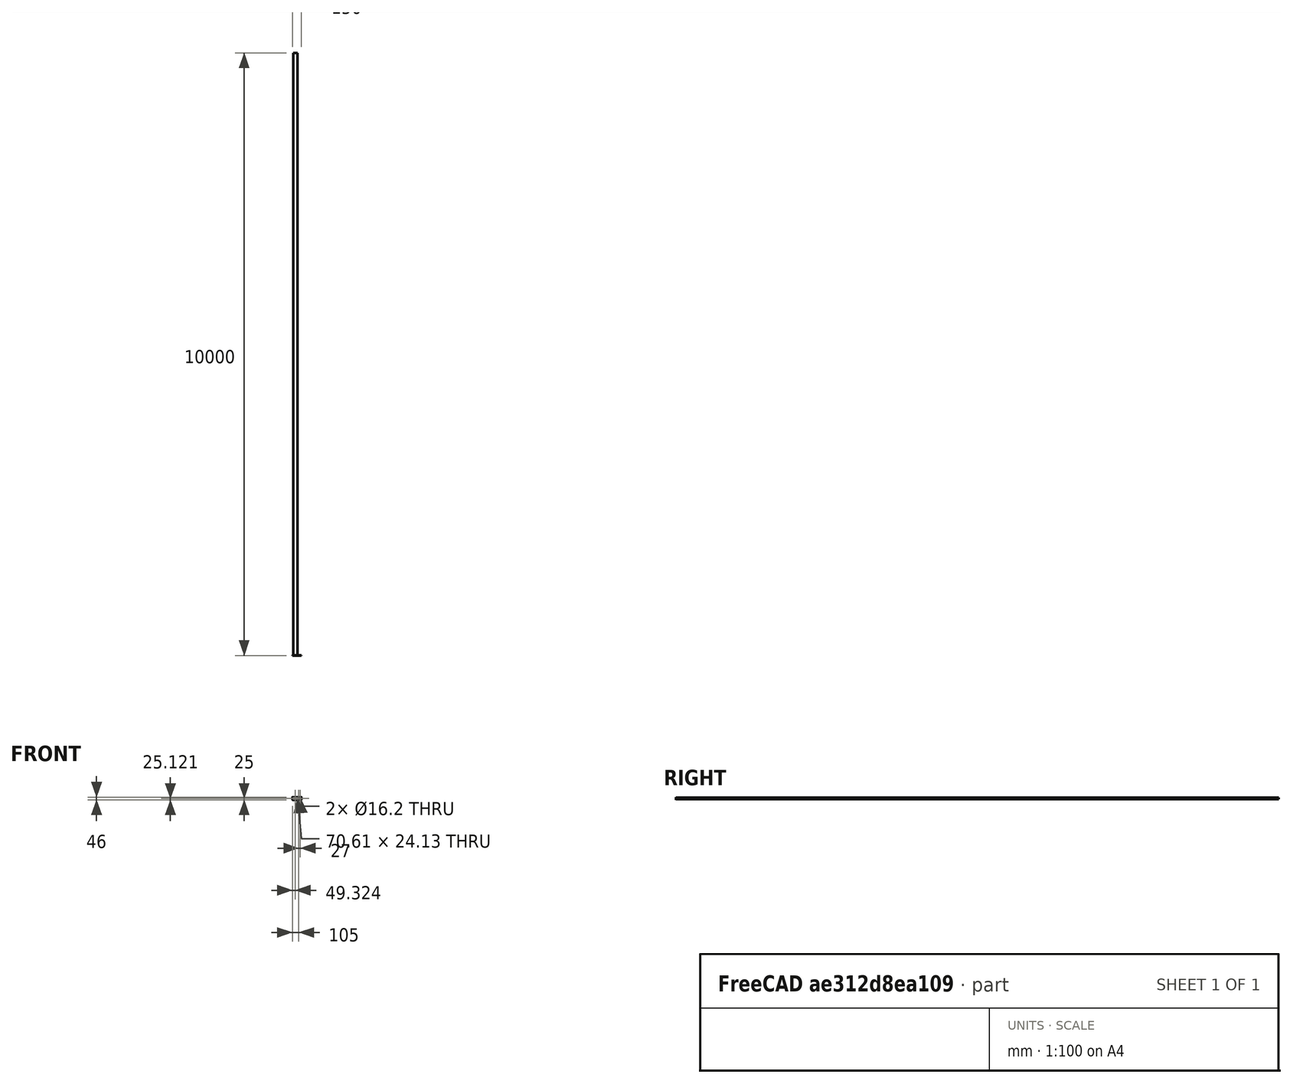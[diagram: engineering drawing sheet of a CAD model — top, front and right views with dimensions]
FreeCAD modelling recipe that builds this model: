
FCSTD DOCUMENT  (FreeCAD 0.14R3702 (Git))
Label: My-Faceplate
License: CC-BY 3.0
LicenseURL: http://creativecommons.org/licenses/by/3.0/
objects: Part::Extrusion×5, Sketcher::SketchObject×4, PartDesign::Fillet×4, PartDesign::Pocket×2, Part::Box×1, Part::MultiFuse×1, Mesh::Feature×1
note: 19 computed .brp shape members not serialized (recipe doc carries the construction recipe); baked Part::Feature solids carry a one-line shape summary decoded from their .brp

FEATURE [Part::Box] Box  label="Cube"
  Height = 46
  Length = 150
  Width = 1.8
FEATURE [Sketcher::SketchObject] Sketch
  Placement = pos=(0,0,0) rot=(1,0,0;1.5708rad)
  Support = -> Box [Face3]
  sketch-geometry (4):
    g0: LineSegment StartX=14.0179 StartY=37.1856 StartZ=0 EndX=84.6299 EndY=37.1856 EndZ=0
    g1: LineSegment StartX=84.6299 StartY=37.1856 StartZ=0 EndX=84.6299 EndY=13.0556 EndZ=0
    g2: LineSegment StartX=84.6299 StartY=13.0556 StartZ=0 EndX=14.0179 EndY=13.0556 EndZ=0
    g3: LineSegment StartX=14.0179 StartY=13.0556 StartZ=0 EndX=14.0179 EndY=37.1856 EndZ=0
  constraints (10):
    c: Coincident(g0,g1)
    c: Coincident(g1,g2)
    c: Coincident(g2,g3)
    c: Coincident(g3,g0)
    c: Horizontal(g0)
    c: Horizontal(g2)
    c: Vertical(g1)
    c: Vertical(g3)
    c: Distance(g2) = 70.612
    c: Distance(g1) = 24.13
FEATURE [PartDesign::Pocket] Pocket
  Length = 5
  Sketch = -> Sketch
  Type = 1
FEATURE [Sketcher::SketchObject] Sketch001
  Placement = pos=(0,0,0) rot=(1,0,0;1.5708rad)
  Support = -> Pocket [Face2]
  sketch-geometry (2):
    g0: Circle CenterX=105 CenterY=25 CenterZ=0 NormalX=0 NormalY=0 NormalZ=1 Radius=8.1
    g1: Circle CenterX=132 CenterY=25 CenterZ=0 NormalX=0 NormalY=0 NormalZ=1 Radius=8.1
  constraints (6):
    c: Radius(g0) = 8.1
    c: Radius(g1) = 8.1
    c: DistanceY(g-1,g0) = 25
    c: DistanceY(g-1,g1) = 25
    c: DistanceX(g-2,g0) = 105
    c: Distance(g0,g1) = 27
FEATURE [PartDesign::Pocket] Pocket001
  Length = 5
  Sketch = -> Sketch001
  Type = 1
FEATURE [PartDesign::Fillet] Fillet
  Base = -> Pocket001 [Edge15]
  Radius = 1.5
FEATURE [PartDesign::Fillet] Fillet001
  Base = -> Fillet [Edge20]
  Radius = 1.5
FEATURE [PartDesign::Fillet] Fillet002
  Base = -> Fillet001 [Edge20]
  Radius = 1.5
FEATURE [PartDesign::Fillet] Fillet003
  Base = -> Fillet002 [Edge22]
  Radius = 1.5
FEATURE [Sketcher::SketchObject] Sketch002
  Placement = pos=(0,1.8,0) rot=(0,0.707107,0.707107;3.14159rad)
  Support = -> Fillet003 [Face16]
  sketch-geometry (4):
    g0: LineSegment StartX=-13.88 StartY=37 StartZ=0 EndX=-8.8 EndY=37 EndZ=0
    g1: LineSegment StartX=-8.8 StartY=37 StartZ=0 EndX=-8.8 EndY=13 EndZ=0
    g2: LineSegment StartX=-8.8 StartY=13 StartZ=0 EndX=-13.88 EndY=13 EndZ=0
    g3: LineSegment StartX=-13.88 StartY=13 StartZ=0 EndX=-13.88 EndY=37 EndZ=0
  constraints (12):
    c: Coincident(g0,g1)
    c: Coincident(g1,g2)
    c: Coincident(g2,g3)
    c: Coincident(g3,g0)
    c: Horizontal(g0)
    c: Horizontal(g2)
    c: Vertical(g1)
    c: Vertical(g3)
    c: Distance(g2) = 5.08
    c: Distance(g1) = 24
    c: DistanceX(g-2,g1) = -8.8
    c: DistanceY(g-1,g1) = 13
FEATURE [Part::Extrusion] Extrude002
  Base = -> Sketch002
  Dir = (0,7.11,0)
  Solid = false
FEATURE [Part::Extrusion] Extrude
  Base = -> Sketch002
  Dir = (0,7.11,0)
  Solid = true
FEATURE [Part::Extrusion] Extrude003
  Base = -> Sketch002
  Dir = (0,7.11,0)
  Solid = true
FEATURE [Sketcher::SketchObject] Sketch003
  Placement = pos=(0,1.8,0) rot=(0,0.707107,0.707107;3.14159rad)
  Support = -> Fillet003 [Face16]
  sketch-geometry (4):
    g0: LineSegment StartX=-90.08 StartY=37 StartZ=0 EndX=-85 EndY=37 EndZ=0
    g1: LineSegment StartX=-85 StartY=37 StartZ=0 EndX=-85 EndY=13 EndZ=0
    g2: LineSegment StartX=-85 StartY=13 StartZ=0 EndX=-90.08 EndY=13 EndZ=0
    g3: LineSegment StartX=-90.08 StartY=13 StartZ=0 EndX=-90.08 EndY=37 EndZ=0
  constraints (12):
    c: Coincident(g0,g1)
    c: Coincident(g1,g2)
    c: Coincident(g2,g3)
    c: Coincident(g3,g0)
    c: Horizontal(g0)
    c: Horizontal(g2)
    c: Vertical(g1)
    c: Vertical(g3)
    c: DistanceY(g-1,g2) = 13
    c: Distance(g2) = 5.08
    c: Distance(g1) = 24
    c: DistanceX(g-2,g1) = -85
FEATURE [Part::Extrusion] Extrude004
  Base = -> Sketch003
  Dir = (0,3.3,0)
  Solid = true
FEATURE [Part::Extrusion] Extrude005
  Base = -> Sketch003
  Dir = (0,3.3,0)
  Solid = true
FEATURE [Part::MultiFuse] Fusion
  Shapes = -> [Fillet003,Extrude,Extrude004]
FEATURE [Mesh::Feature] Mesh  label="Fusion (Meshed)"
